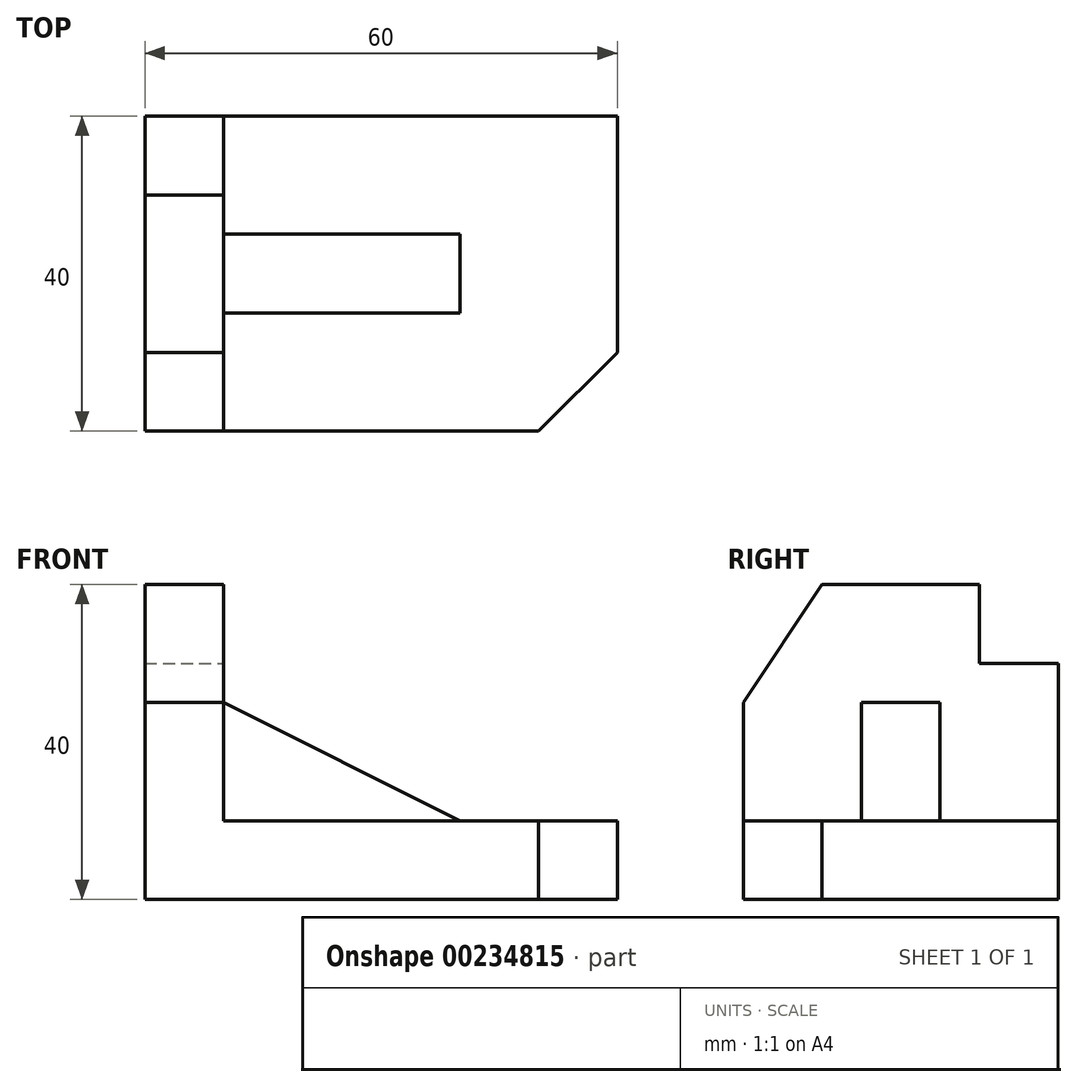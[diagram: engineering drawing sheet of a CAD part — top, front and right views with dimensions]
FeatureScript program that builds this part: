
annotation { "Feature Type Name" : "Feature", "Feature Type Description" : "" }
export const myFeature = defineFeature(function(context is Context, id is Id, definition is map)
    precondition{}
    {
        {
            var Q0;
            Q0=qCreatedBy(makeId("Front.planeOp"),FACE);
            var sketch = newSketch(context, id + "F0", { "sketchPlane" : qUnion([Q0])});
            skLineSegment(sketch, "E0.bottom", {"start": v(0, 40) * mm, "end": v(60, 40) * mm});
            skLineSegment(sketch, "E0.top", {"start": v(0, 0) * mm, "end": v(60, 0) * mm});
            skLineSegment(sketch, "E0.left", {"start": v(0, 40) * mm, "end": v(0, 0) * mm});
            skLineSegment(sketch, "E0.right", {"start": v(60, 40) * mm, "end": v(60, 0) * mm});
            skSolve(sketch);
        }
        {
            var Q0;
            Q0 = qSketchRegion(id + "F0", true);
            extrude(context, id + "F1", {"entities" : qUnion([Q0]), "oppositeDirection" : true, "depth" : 40 * mm});
        }
        {
            var Q0;
            Q0=makeQuery(id+"F1.opExtrude","CAP_FACE",FACE,{"disambiguationData":[OSD([sQuery(id+"F0.wireOp",EDGE,"E0.bottom"),sQuery(id+"F0.wireOp",EDGE,"E0.top"),sQuery(id+"F0.wireOp",EDGE,"E0.left"),sQuery(id+"F0.wireOp",EDGE,"E0.right")])],"isStart":true});
            var sketch = newSketch(context, id + "F2", { "sketchPlane" : qUnion([Q0])});
            skLineSegment(sketch, "E1.bottom", {"start": v(10, 50) * mm, "end": v(70, 50) * mm});
            skLineSegment(sketch, "E1.top", {"start": v(10, 10) * mm, "end": v(70, 10) * mm});
            skLineSegment(sketch, "E1.left", {"start": v(10, 50) * mm, "end": v(10, 10) * mm});
            skLineSegment(sketch, "E1.right", {"start": v(70, 50) * mm, "end": v(70, 10) * mm});
            skSolve(sketch);
        }
        {
            var Q0;
            Q0 = qSketchRegion(id + "F2", true);
            extrude(context, id + "F3", {"entities" : qUnion([Q0]), "operationType" : NewBodyOperationType.REMOVE, "endBound" : BoundingType.THROUGH_ALL, "oppositeDirection" : true, "depth" : 25 * mm});
        }
        {
            var Q0;
            Q0=makeQuery(id+"F3.boolean.opBoolean","COPY",FACE,{"derivedFrom":makeQuery(id+"F3.opExtrude","SWEPT_FACE",FACE,{"disambiguationData":[OSD([sQuery(id+"F2.wireOp",EDGE,"E1.left")])]})});
            var sketch = newSketch(context, id + "F4", { "sketchPlane" : qUnion([Q0])});
            skLineSegment(sketch, "E2", {"start": v(0, 25) * mm, "end": v(10, 40) * mm});
            skLineSegment(sketch, "E3", {"start": v(10, 40) * mm, "end": v(10, 50) * mm});
            skLineSegment(sketch, "E4", {"start": v(10, 50) * mm, "end": v(-10, 50) * mm});
            skLineSegment(sketch, "E5", {"start": v(-10, 50) * mm, "end": v(-10, 25) * mm});
            skLineSegment(sketch, "E6", {"start": v(-10, 25) * mm, "end": v(0, 25) * mm});
            skSolve(sketch);
        }
        {
            var Q0;
            Q0 = qSketchRegion(id + "F4", true);
            extrude(context, id + "F5", {"entities" : qUnion([Q0]), "operationType" : NewBodyOperationType.REMOVE, "endBound" : BoundingType.THROUGH_ALL, "oppositeDirection" : true, "depth" : 25 * mm});
        }
        {
            var Q0;
            Q0=makeQuery(id+"F3.boolean.opBoolean","COPY",FACE,{"derivedFrom":makeQuery(id+"F3.opExtrude","SWEPT_FACE",FACE,{"disambiguationData":[OSD([sQuery(id+"F2.wireOp",EDGE,"E1.left")])]})});
            var sketch = newSketch(context, id + "F6", { "sketchPlane" : qUnion([Q0])});
            skLineSegment(sketch, "E7.bottom", {"start": v(30, 50) * mm, "end": v(50, 50) * mm});
            skLineSegment(sketch, "E7.top", {"start": v(30, 30) * mm, "end": v(50, 30) * mm});
            skLineSegment(sketch, "E7.left", {"start": v(30, 50) * mm, "end": v(30, 30) * mm});
            skLineSegment(sketch, "E7.right", {"start": v(50, 50) * mm, "end": v(50, 30) * mm});
            skSolve(sketch);
        }
        {
            var Q0;
            Q0 = qSketchRegion(id + "F6", true);
            extrude(context, id + "F7", {"entities" : qUnion([Q0]), "operationType" : NewBodyOperationType.REMOVE, "endBound" : BoundingType.THROUGH_ALL, "oppositeDirection" : true, "depth" : 25 * mm});
        }
        {
            var Q0;
            Q0=makeQuery(id+"F3.boolean.opBoolean","COPY",FACE,{"derivedFrom":makeQuery(id+"F3.opExtrude","SWEPT_FACE",FACE,{"disambiguationData":[OSD([sQuery(id+"F2.wireOp",EDGE,"E1.top")])]})});
            var sketch = newSketch(context, id + "F8", { "sketchPlane" : qUnion([Q0])});
            skLineSegment(sketch, "E8", {"start": v(50, 0) * mm, "end": v(60, 10) * mm});
            skLineSegment(sketch, "E9", {"start": v(60, 10) * mm, "end": v(70, 10) * mm});
            skLineSegment(sketch, "E10", {"start": v(70, 10) * mm, "end": v(70, -10) * mm});
            skLineSegment(sketch, "E11", {"start": v(70, -10) * mm, "end": v(50, -10) * mm});
            skLineSegment(sketch, "E12", {"start": v(50, -10) * mm, "end": v(50, 0) * mm});
            skSolve(sketch);
        }
        {
            var Q0;
            Q0 = qSketchRegion(id + "F8", true);
            extrude(context, id + "F9", {"entities" : qUnion([Q0]), "operationType" : NewBodyOperationType.REMOVE, "endBound" : BoundingType.THROUGH_ALL, "oppositeDirection" : true, "depth" : 25 * mm});
        }
        {
            var Q0;
            Q0=qCreatedBy(makeId("Front.planeOp"),FACE);
            cPlane(context, id + "F10", {"entities" : qUnion([Q0]), "cplaneType" : CPlaneType.OFFSET, "offset" : 25 * mm, "oppositeDirection" : true, "width" : 150 * mm, "height" : 150 * mm});
        }
        {
            var Q0;
            Q0=qCreatedBy(id+"F10.planeOp",FACE);
            var sketch = newSketch(context, id + "F11", { "sketchPlane" : qUnion([Q0])});
            skLineSegment(sketch, "E13", {"start": v(10, 25) * mm, "end": v(40, 10) * mm});
            skLineSegment(sketch, "E14", {"start": v(40, 10) * mm, "end": v(40, 5) * mm});
            skLineSegment(sketch, "E15", {"start": v(40, 5) * mm, "end": v(5, 5) * mm});
            skLineSegment(sketch, "E16", {"start": v(5, 5) * mm, "end": v(5, 25) * mm});
            skLineSegment(sketch, "E17", {"start": v(5, 25) * mm, "end": v(10, 25) * mm});
            skSolve(sketch);
        }
        {
            var Q0;
            Q0 = qSketchRegion(id + "F11", true);
            extrude(context, id + "F12", {"entities" : qUnion([Q0]), "operationType" : NewBodyOperationType.ADD, "depth" : 10 * mm});
        }
    });
